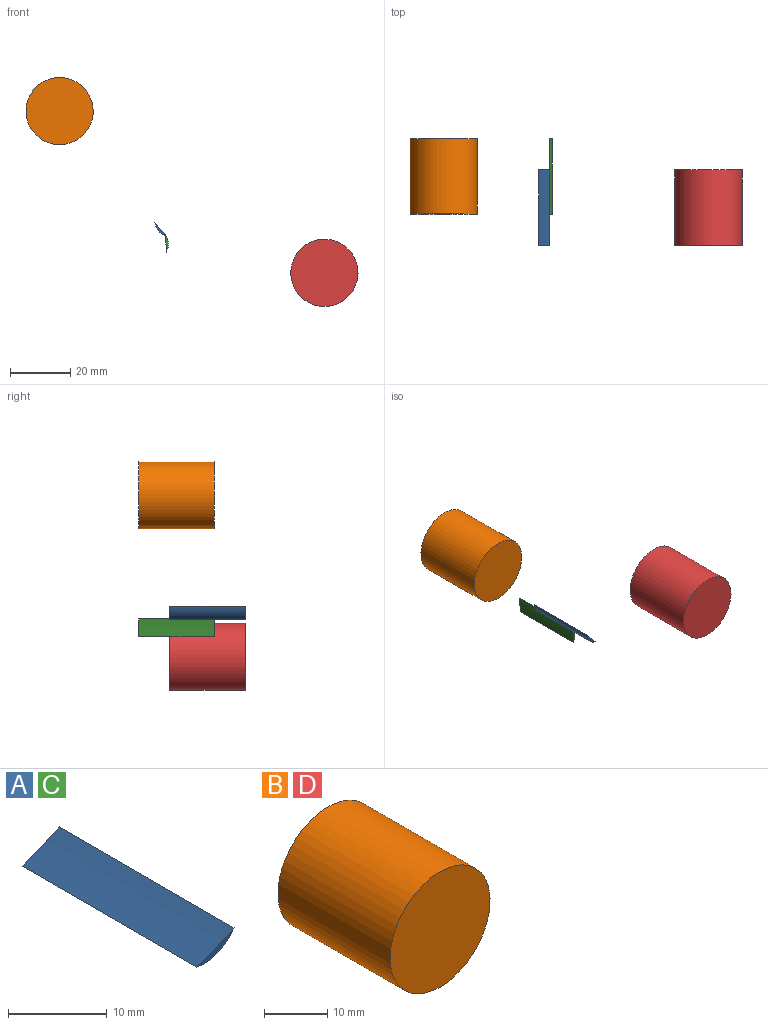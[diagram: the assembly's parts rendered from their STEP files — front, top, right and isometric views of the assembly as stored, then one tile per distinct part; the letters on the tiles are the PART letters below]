
ASSEMBLY  parts=4 mates=2
PART A: 4 faces, bbox 5.3x25x2.3 mm
  f0: cylinder r=47.75mm len=25mm, axis (0,1,0), area 143.7mm2, adj f1,f2,f3
  f1: cylinder r=5.14mm len=25mm, axis (0,1,0), area 152.4mm2, adj f0,f2,f3
  f2: plane 5.31x2.3mm, normal (0,-1,0), area 3.1mm2, adj f0,f1
  f3: plane 5.31x2.3mm, normal (0,1,0), area 3.1mm2, adj f0,f1
PART B: 3 faces, bbox 22.3x25x22.3 mm
  f0: cylinder r=11.14mm len=25mm, axis (0,1,0), area 1749.5mm2, adj f1,f2
  f1: plane 22.28x22.28mm, normal (0,-1,0), area 389.7mm2, adj f0
  f2: plane 22.28x22.28mm, normal (0,1,0), area 389.7mm2, adj f0
PART C: same geometry as A
PART D: same geometry as B
PLACE A rot(axis=(0,1,0),73.1deg) t=(-65.81,5.71,8.67)mm
PLACE B t=(-136.07,16,17.54)mm fixed
PLACE C rot(axis=(0,-1,0),70.5deg) t=(-148.49,16,-28.88)mm
PLACE D rot(axis=(0,1,0),2.6deg) t=(-48.27,5.71,-36.07)mm fixed
MATE revolute D.f0 <-> A.f2  axis (0,-1,0) through (-48.27,-19.29,-36.07)mm
MATE revolute C.f2 <-> B.f0  axis (0,-1,0) through (-136.07,-9,17.54)mm
